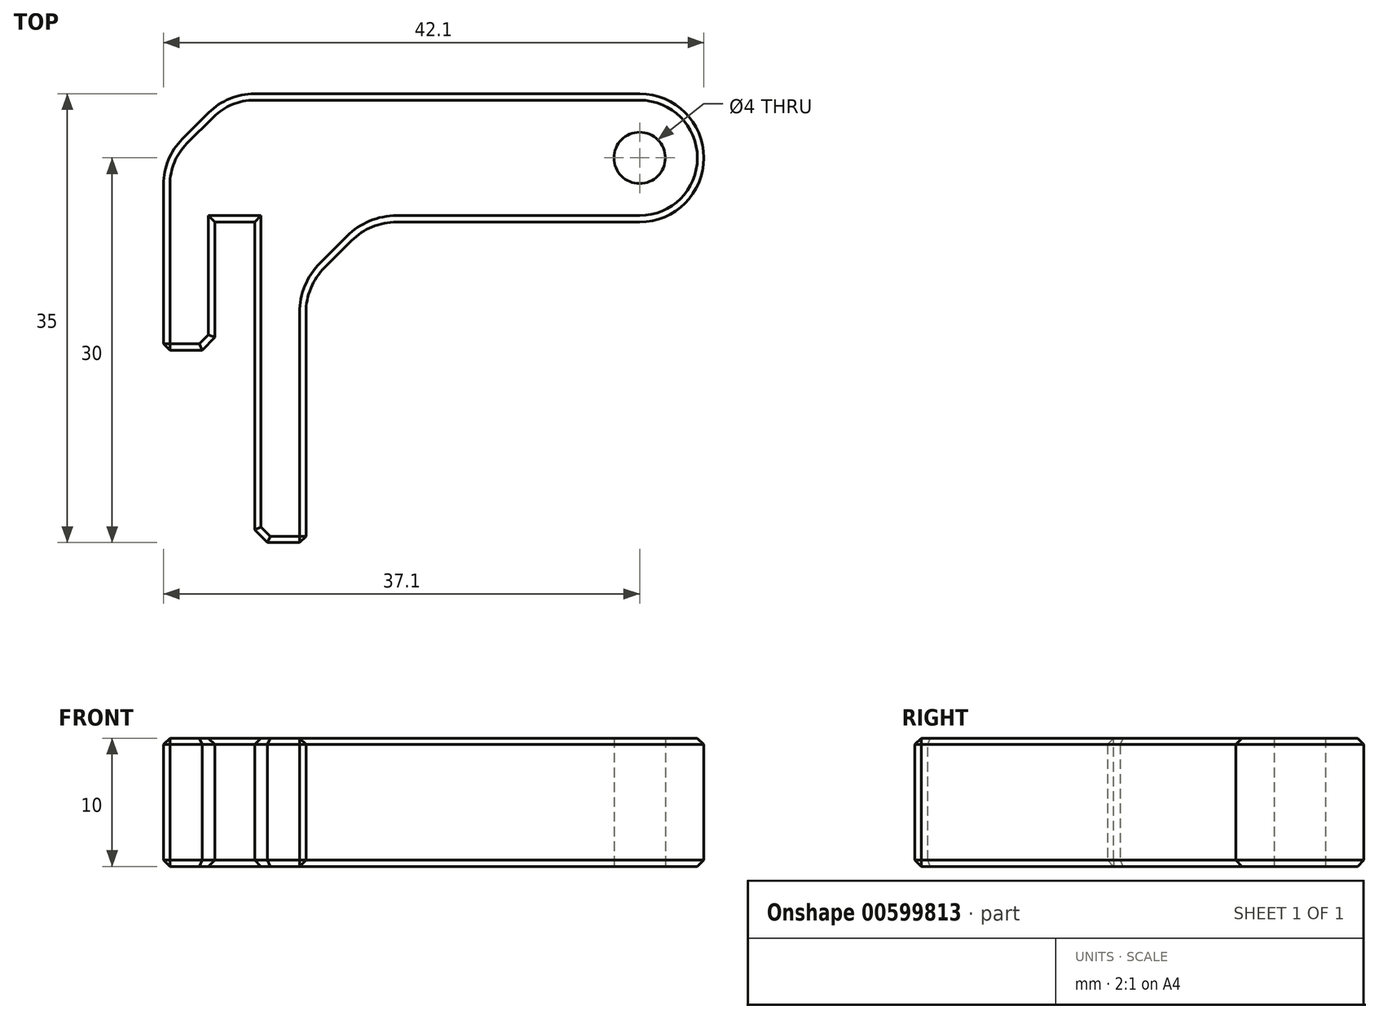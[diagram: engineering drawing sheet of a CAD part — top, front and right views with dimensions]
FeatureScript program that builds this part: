
annotation { "Feature Type Name" : "Feature", "Feature Type Description" : "" }
export const myFeature = defineFeature(function(context is Context, id is Id, definition is map)
    precondition{}
    {
        {
            var Q0;
            Q0=qCreatedBy(makeId("Top.planeOp"),FACE);
            var sketch = newSketch(context, id + "F0", { "sketchPlane" : qUnion([Q0])});
            skLineSegment(sketch, "E0", {"start": v(0, 0) * mm, "end": v(0, 20) * mm});
            skLineSegment(sketch, "E1", {"start": v(0, 0) * mm, "end": v(4, 0) * mm});
            skLineSegment(sketch, "E2", {"start": v(4, 0) * mm, "end": v(4, 10) * mm});
            skLineSegment(sketch, "E3", {"start": v(4, 10) * mm, "end": v(7.1, 10) * mm});
            skLineSegment(sketch, "E4", {"start": v(7.1, 10) * mm, "end": v(7.1, -15) * mm});
            skLineSegment(sketch, "E5", {"start": v(7.1, -15) * mm, "end": v(11.1, -15) * mm});
            skLineSegment(sketch, "E6", {"start": v(37.1, 10) * mm, "end": v(11.1, 10) * mm});
            skLineSegment(sketch, "E7", {"start": v(11.1, 10) * mm, "end": v(11.1, -15) * mm});
            skLineSegment(sketch, "E8", {"start": v(0, 20) * mm, "end": v(37.1, 20) * mm});
            skArc(sketch, "E9", {"start": v(37.1, 10) * mm, "mid": v(42.1, 15) * mm, "end": v(37.1, 20) * mm});
            skCircle(sketch, "E10", {"center": v(37.1, 15) * mm, "radius": 2 * mm});
            skSolve(sketch);
        }
        {
            var Q0;
            Q0=makeQuery(id+"F0.imprint","IMPRINT",FACE,{"disambiguationData":[TD([[makeQuery(id+"F0.imprint","IMPRINT",EDGE,{"derivedFrom":sQuery(id+"F0.wireOp",EDGE,"E0")}),-1.0]])]});
            extrude(context, id + "F1", {"entities" : qUnion([Q0]), "depth" : 10 * mm, "offsetDistance" : 25 * mm});
        }
        {
            var Q0;
            Q0=makeQuery(id+"F1.opExtrude","SWEPT_EDGE",EDGE,{"disambiguationData":[OSD([sQuery(id+"F0.wireOp",EDGE,"E0"),sQuery(id+"F0.wireOp",EDGE,"E8")])]});
            var Q1;
            Q1=makeQuery(id+"F1.opExtrude","SWEPT_EDGE",EDGE,{"disambiguationData":[OSD([sQuery(id+"F0.wireOp",EDGE,"E6"),sQuery(id+"F0.wireOp",EDGE,"E7")])]});
            chamfer(context, id + "F2", {"entities" : qUnion([Q0, Q1]), "width" : 5 * mm, "tangentPropagation" : true});
        }
        {
            var Q0;
            {var subQ0=sQuery(id+"F0.wireOp",EDGE,"E0");Q0=makeQuery(id+"F2.opChamfer","BLEND_EDGE",EDGE,{"blendedFrom":[makeQuery(id+"F1.opExtrude","SWEPT_EDGE",EDGE,{"disambiguationData":[OSD([subQ0,sQuery(id+"F0.wireOp",EDGE,"E8")])]}),makeQuery(id+"F1.opExtrude","SWEPT_FACE",FACE,{"disambiguationData":[OSD([subQ0])]})],"blendedInto":[makeQuery(id+"F1.opExtrude","SWEPT_FACE",FACE,{"disambiguationData":[OSD([subQ0])]})]});}
            var Q1;
            {var subQ0=sQuery(id+"F0.wireOp",EDGE,"E8");Q1=makeQuery(id+"F2.opChamfer","BLEND_EDGE",EDGE,{"blendedFrom":[makeQuery(id+"F1.opExtrude","SWEPT_EDGE",EDGE,{"disambiguationData":[OSD([sQuery(id+"F0.wireOp",EDGE,"E0"),subQ0])]}),makeQuery(id+"F1.opExtrude","SWEPT_FACE",FACE,{"disambiguationData":[OSD([subQ0])]})],"blendedInto":[makeQuery(id+"F1.opExtrude","SWEPT_FACE",FACE,{"disambiguationData":[OSD([subQ0])]})]});}
            var Q2;
            {var subQ0=sQuery(id+"F0.wireOp",EDGE,"E6");Q2=makeQuery(id+"F2.opChamfer","BLEND_EDGE",EDGE,{"blendedFrom":[makeQuery(id+"F1.opExtrude","SWEPT_EDGE",EDGE,{"disambiguationData":[OSD([subQ0,sQuery(id+"F0.wireOp",EDGE,"E7")])]}),makeQuery(id+"F1.opExtrude","SWEPT_FACE",FACE,{"disambiguationData":[OSD([subQ0])]})],"blendedInto":[makeQuery(id+"F1.opExtrude","SWEPT_FACE",FACE,{"disambiguationData":[OSD([subQ0])]})]});}
            var Q3;
            {var subQ0=sQuery(id+"F0.wireOp",EDGE,"E7");Q3=makeQuery(id+"F2.opChamfer","BLEND_EDGE",EDGE,{"blendedFrom":[makeQuery(id+"F1.opExtrude","SWEPT_EDGE",EDGE,{"disambiguationData":[OSD([sQuery(id+"F0.wireOp",EDGE,"E6"),subQ0])]}),makeQuery(id+"F1.opExtrude","SWEPT_FACE",FACE,{"disambiguationData":[OSD([subQ0])]})],"blendedInto":[makeQuery(id+"F1.opExtrude","SWEPT_FACE",FACE,{"disambiguationData":[OSD([subQ0])]})]});}
            fillet(context, id + "F3", {"entities" : qUnion([Q0, Q1, Q2, Q3]), "radius" : 5 * mm, "tangentPropagation" : true, "allowEdgeOverflow" : false});
        }
        {
            var Q0;
            Q0=makeQuery(id+"F1.opExtrude","SWEPT_EDGE",EDGE,{"disambiguationData":[OSD([sQuery(id+"F0.wireOp",EDGE,"E1"),sQuery(id+"F0.wireOp",EDGE,"E2")])]});
            var Q1;
            Q1=makeQuery(id+"F1.opExtrude","SWEPT_EDGE",EDGE,{"disambiguationData":[OSD([sQuery(id+"F0.wireOp",EDGE,"E4"),sQuery(id+"F0.wireOp",EDGE,"E5")])]});
            chamfer(context, id + "F4", {"entities" : qUnion([Q0, Q1]), "width" : 1 * mm, "tangentPropagation" : true});
        }
        {
            var Q0;
            Q0=makeQuery(id+"F1.opExtrude","SWEPT_EDGE",EDGE,{"disambiguationData":[OSD([sQuery(id+"F0.wireOp",EDGE,"E0"),sQuery(id+"F0.wireOp",EDGE,"E1")])]});
            var Q1;
            Q1=makeQuery(id+"F1.opExtrude","SWEPT_EDGE",EDGE,{"disambiguationData":[OSD([sQuery(id+"F0.wireOp",EDGE,"E5"),sQuery(id+"F0.wireOp",EDGE,"E7")])]});
            var Q2;
            Q2=makeQuery(id+"F1.opExtrude","CAP_EDGE",EDGE,{"disambiguationData":[OSD([sQuery(id+"F0.wireOp",EDGE,"E6")])],"isStart":false});
            var Q3;
            Q3=makeQuery(id+"F1.opExtrude","CAP_EDGE",EDGE,{"disambiguationData":[OSD([sQuery(id+"F0.wireOp",EDGE,"E6")])],"isStart":true});
            var Q4;
            Q4=makeQuery(id+"F1.opExtrude","CAP_EDGE",EDGE,{"disambiguationData":[OSD([sQuery(id+"F0.wireOp",EDGE,"E1")])],"isStart":false});
            var Q5;
            {var subQ0=sQuery(id+"F0.wireOp",EDGE,"E2");var subQ1=sQuery(id+"F0.wireOp",EDGE,"E1");Q5=makeQuery(id+"F4.opChamfer","BLEND_EDGE",EDGE,{"blendedFrom":[makeQuery(id+"F1.opExtrude","SWEPT_EDGE",EDGE,{"disambiguationData":[OSD([subQ1,subQ0])]}),makeQuery(id+"F1.opExtrude","CAP_FACE",FACE,{"disambiguationData":[OSD([sQuery(id+"F0.wireOp",EDGE,"E0"),subQ1,subQ0,sQuery(id+"F0.wireOp",EDGE,"E3"),sQuery(id+"F0.wireOp",EDGE,"E4"),sQuery(id+"F0.wireOp",EDGE,"E5"),sQuery(id+"F0.wireOp",EDGE,"E6"),sQuery(id+"F0.wireOp",EDGE,"E7"),sQuery(id+"F0.wireOp",EDGE,"E8"),sQuery(id+"F0.wireOp",EDGE,"E9"),sQuery(id+"F0.wireOp",EDGE,"E10")])],"isStart":false})],"blendedInto":[makeQuery(id+"F1.opExtrude","CAP_FACE",FACE,{"disambiguationData":[OSD([sQuery(id+"F0.wireOp",EDGE,"E0"),subQ1,subQ0,sQuery(id+"F0.wireOp",EDGE,"E3"),sQuery(id+"F0.wireOp",EDGE,"E4"),sQuery(id+"F0.wireOp",EDGE,"E5"),sQuery(id+"F0.wireOp",EDGE,"E6"),sQuery(id+"F0.wireOp",EDGE,"E7"),sQuery(id+"F0.wireOp",EDGE,"E8"),sQuery(id+"F0.wireOp",EDGE,"E9"),sQuery(id+"F0.wireOp",EDGE,"E10")])],"isStart":false})]});}
            var Q6;
            Q6=makeQuery(id+"F1.opExtrude","CAP_EDGE",EDGE,{"disambiguationData":[OSD([sQuery(id+"F0.wireOp",EDGE,"E2")])],"isStart":false});
            var Q7;
            Q7=makeQuery(id+"F1.opExtrude","CAP_EDGE",EDGE,{"disambiguationData":[OSD([sQuery(id+"F0.wireOp",EDGE,"E3")])],"isStart":false});
            var Q8;
            Q8=makeQuery(id+"F1.opExtrude","CAP_EDGE",EDGE,{"disambiguationData":[OSD([sQuery(id+"F0.wireOp",EDGE,"E4")])],"isStart":false});
            var Q9;
            Q9=makeQuery(id+"F1.opExtrude","CAP_EDGE",EDGE,{"disambiguationData":[OSD([sQuery(id+"F0.wireOp",EDGE,"E5")])],"isStart":false});
            var Q10;
            {var subQ0=sQuery(id+"F0.wireOp",EDGE,"E5");var subQ1=sQuery(id+"F0.wireOp",EDGE,"E4");Q10=makeQuery(id+"F4.opChamfer","BLEND_EDGE",EDGE,{"blendedFrom":[makeQuery(id+"F1.opExtrude","SWEPT_EDGE",EDGE,{"disambiguationData":[OSD([subQ1,subQ0])]}),makeQuery(id+"F1.opExtrude","CAP_FACE",FACE,{"disambiguationData":[OSD([sQuery(id+"F0.wireOp",EDGE,"E0"),sQuery(id+"F0.wireOp",EDGE,"E1"),sQuery(id+"F0.wireOp",EDGE,"E2"),sQuery(id+"F0.wireOp",EDGE,"E3"),subQ1,subQ0,sQuery(id+"F0.wireOp",EDGE,"E6"),sQuery(id+"F0.wireOp",EDGE,"E7"),sQuery(id+"F0.wireOp",EDGE,"E8"),sQuery(id+"F0.wireOp",EDGE,"E9"),sQuery(id+"F0.wireOp",EDGE,"E10")])],"isStart":false})],"blendedInto":[makeQuery(id+"F1.opExtrude","CAP_FACE",FACE,{"disambiguationData":[OSD([sQuery(id+"F0.wireOp",EDGE,"E0"),sQuery(id+"F0.wireOp",EDGE,"E1"),sQuery(id+"F0.wireOp",EDGE,"E2"),sQuery(id+"F0.wireOp",EDGE,"E3"),subQ1,subQ0,sQuery(id+"F0.wireOp",EDGE,"E6"),sQuery(id+"F0.wireOp",EDGE,"E7"),sQuery(id+"F0.wireOp",EDGE,"E8"),sQuery(id+"F0.wireOp",EDGE,"E9"),sQuery(id+"F0.wireOp",EDGE,"E10")])],"isStart":false})]});}
            var Q11;
            Q11=makeQuery(id+"F1.opExtrude","CAP_EDGE",EDGE,{"disambiguationData":[OSD([sQuery(id+"F0.wireOp",EDGE,"E1")])],"isStart":true});
            var Q12;
            {var subQ0=sQuery(id+"F0.wireOp",EDGE,"E2");var subQ1=sQuery(id+"F0.wireOp",EDGE,"E1");Q12=makeQuery(id+"F4.opChamfer","BLEND_EDGE",EDGE,{"blendedFrom":[makeQuery(id+"F1.opExtrude","SWEPT_EDGE",EDGE,{"disambiguationData":[OSD([subQ1,subQ0])]}),makeQuery(id+"F1.opExtrude","CAP_FACE",FACE,{"disambiguationData":[OSD([sQuery(id+"F0.wireOp",EDGE,"E0"),subQ1,subQ0,sQuery(id+"F0.wireOp",EDGE,"E3"),sQuery(id+"F0.wireOp",EDGE,"E4"),sQuery(id+"F0.wireOp",EDGE,"E5"),sQuery(id+"F0.wireOp",EDGE,"E6"),sQuery(id+"F0.wireOp",EDGE,"E7"),sQuery(id+"F0.wireOp",EDGE,"E8"),sQuery(id+"F0.wireOp",EDGE,"E9"),sQuery(id+"F0.wireOp",EDGE,"E10")])],"isStart":true})],"blendedInto":[makeQuery(id+"F1.opExtrude","CAP_FACE",FACE,{"disambiguationData":[OSD([sQuery(id+"F0.wireOp",EDGE,"E0"),subQ1,subQ0,sQuery(id+"F0.wireOp",EDGE,"E3"),sQuery(id+"F0.wireOp",EDGE,"E4"),sQuery(id+"F0.wireOp",EDGE,"E5"),sQuery(id+"F0.wireOp",EDGE,"E6"),sQuery(id+"F0.wireOp",EDGE,"E7"),sQuery(id+"F0.wireOp",EDGE,"E8"),sQuery(id+"F0.wireOp",EDGE,"E9"),sQuery(id+"F0.wireOp",EDGE,"E10")])],"isStart":true})]});}
            var Q13;
            Q13=makeQuery(id+"F1.opExtrude","CAP_EDGE",EDGE,{"disambiguationData":[OSD([sQuery(id+"F0.wireOp",EDGE,"E2")])],"isStart":true});
            var Q14;
            Q14=makeQuery(id+"F1.opExtrude","CAP_EDGE",EDGE,{"disambiguationData":[OSD([sQuery(id+"F0.wireOp",EDGE,"E3")])],"isStart":true});
            var Q15;
            Q15=makeQuery(id+"F1.opExtrude","CAP_EDGE",EDGE,{"disambiguationData":[OSD([sQuery(id+"F0.wireOp",EDGE,"E4")])],"isStart":true});
            var Q16;
            {var subQ0=sQuery(id+"F0.wireOp",EDGE,"E5");var subQ1=sQuery(id+"F0.wireOp",EDGE,"E4");Q16=makeQuery(id+"F4.opChamfer","BLEND_EDGE",EDGE,{"blendedFrom":[makeQuery(id+"F1.opExtrude","SWEPT_EDGE",EDGE,{"disambiguationData":[OSD([subQ1,subQ0])]}),makeQuery(id+"F1.opExtrude","CAP_FACE",FACE,{"disambiguationData":[OSD([sQuery(id+"F0.wireOp",EDGE,"E0"),sQuery(id+"F0.wireOp",EDGE,"E1"),sQuery(id+"F0.wireOp",EDGE,"E2"),sQuery(id+"F0.wireOp",EDGE,"E3"),subQ1,subQ0,sQuery(id+"F0.wireOp",EDGE,"E6"),sQuery(id+"F0.wireOp",EDGE,"E7"),sQuery(id+"F0.wireOp",EDGE,"E8"),sQuery(id+"F0.wireOp",EDGE,"E9"),sQuery(id+"F0.wireOp",EDGE,"E10")])],"isStart":true})],"blendedInto":[makeQuery(id+"F1.opExtrude","CAP_FACE",FACE,{"disambiguationData":[OSD([sQuery(id+"F0.wireOp",EDGE,"E0"),sQuery(id+"F0.wireOp",EDGE,"E1"),sQuery(id+"F0.wireOp",EDGE,"E2"),sQuery(id+"F0.wireOp",EDGE,"E3"),subQ1,subQ0,sQuery(id+"F0.wireOp",EDGE,"E6"),sQuery(id+"F0.wireOp",EDGE,"E7"),sQuery(id+"F0.wireOp",EDGE,"E8"),sQuery(id+"F0.wireOp",EDGE,"E9"),sQuery(id+"F0.wireOp",EDGE,"E10")])],"isStart":true})]});}
            var Q17;
            Q17=makeQuery(id+"F1.opExtrude","CAP_EDGE",EDGE,{"disambiguationData":[OSD([sQuery(id+"F0.wireOp",EDGE,"E5")])],"isStart":true});
            chamfer(context, id + "F5", {"entities" : qUnion([Q0, Q1, Q2, Q3, Q4, Q5, Q6, Q7, Q8, Q9, Q10, Q11, Q12, Q13, Q14, Q15, Q16, Q17]), "width" : .5 * mm, "tangentPropagation" : true});
        }
    });
